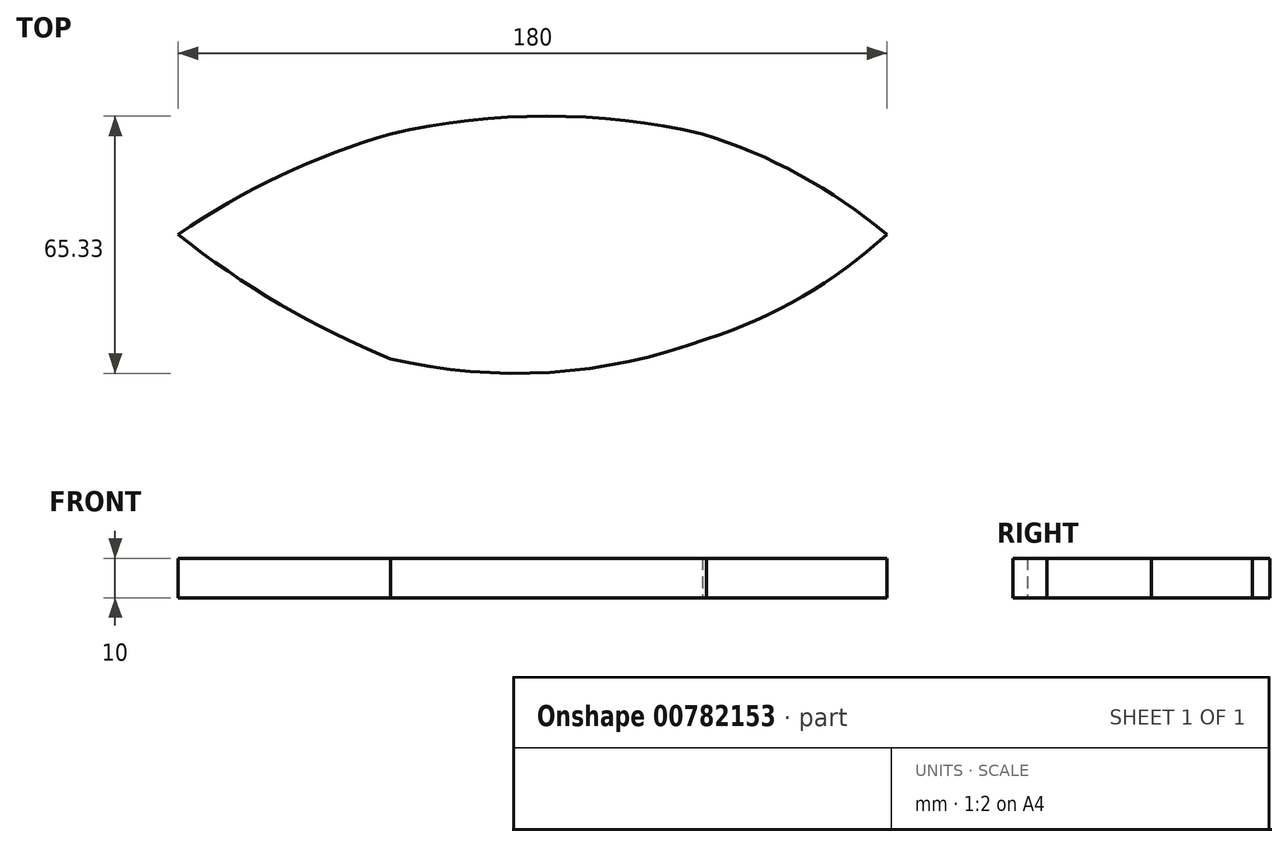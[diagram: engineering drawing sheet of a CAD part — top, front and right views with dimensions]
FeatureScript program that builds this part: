
annotation { "Feature Type Name" : "Feature", "Feature Type Description" : "" }
export const myFeature = defineFeature(function(context is Context, id is Id, definition is map)
    precondition{}
    {
        {
            var Q0;
            Q0=qCreatedBy(makeId("Top.planeOp"),FACE);
            var sketch = newSketch(context, id + "F0", { "sketchPlane" : qUnion([Q0])});
            skLineSegment(sketch, "E0", {"start": v(90.2, 0) * mm, "end": v(-89.8, 0) * mm});
            skArc(sketch, "E1", {"start": v(-89.8, 0) * mm, "mid": v(-63.96, -17.74) * mm, "end": v(-35.84, -31.58) * mm});
            skArc(sketch, "E2", {"start": v(-35.84, 25.56) * mm, "mid": v(-63.87, 15) * mm, "end": v(-89.8, 0) * mm});
            skArc(sketch, "E3", {"start": v(43.36, 25.56) * mm, "mid": v(3.76, 30.06) * mm, "end": v(-35.84, 25.56) * mm});
            skArc(sketch, "E4", {"start": v(90.2, 0) * mm, "mid": v(68.06, 15.13) * mm, "end": v(43.36, 25.56) * mm});
            skArc(sketch, "E5", {"start": v(44.36, -26.56) * mm, "mid": v(68.72, -15.77) * mm, "end": v(90.2, 0) * mm});
            skArc(sketch, "E6", {"start": v(-35.84, -31.58) * mm, "mid": v(4.63, -35) * mm, "end": v(44.36, -26.56) * mm});
            skSolve(sketch);
        }
        {
            var Q0;
            Q0 = qSketchRegion(id + "F0", true);
            extrude(context, id + "F1", {"entities" : qUnion([Q0]), "depth" : 10 * mm, "offsetDistance" : 25.4 * mm});
        }
    });
